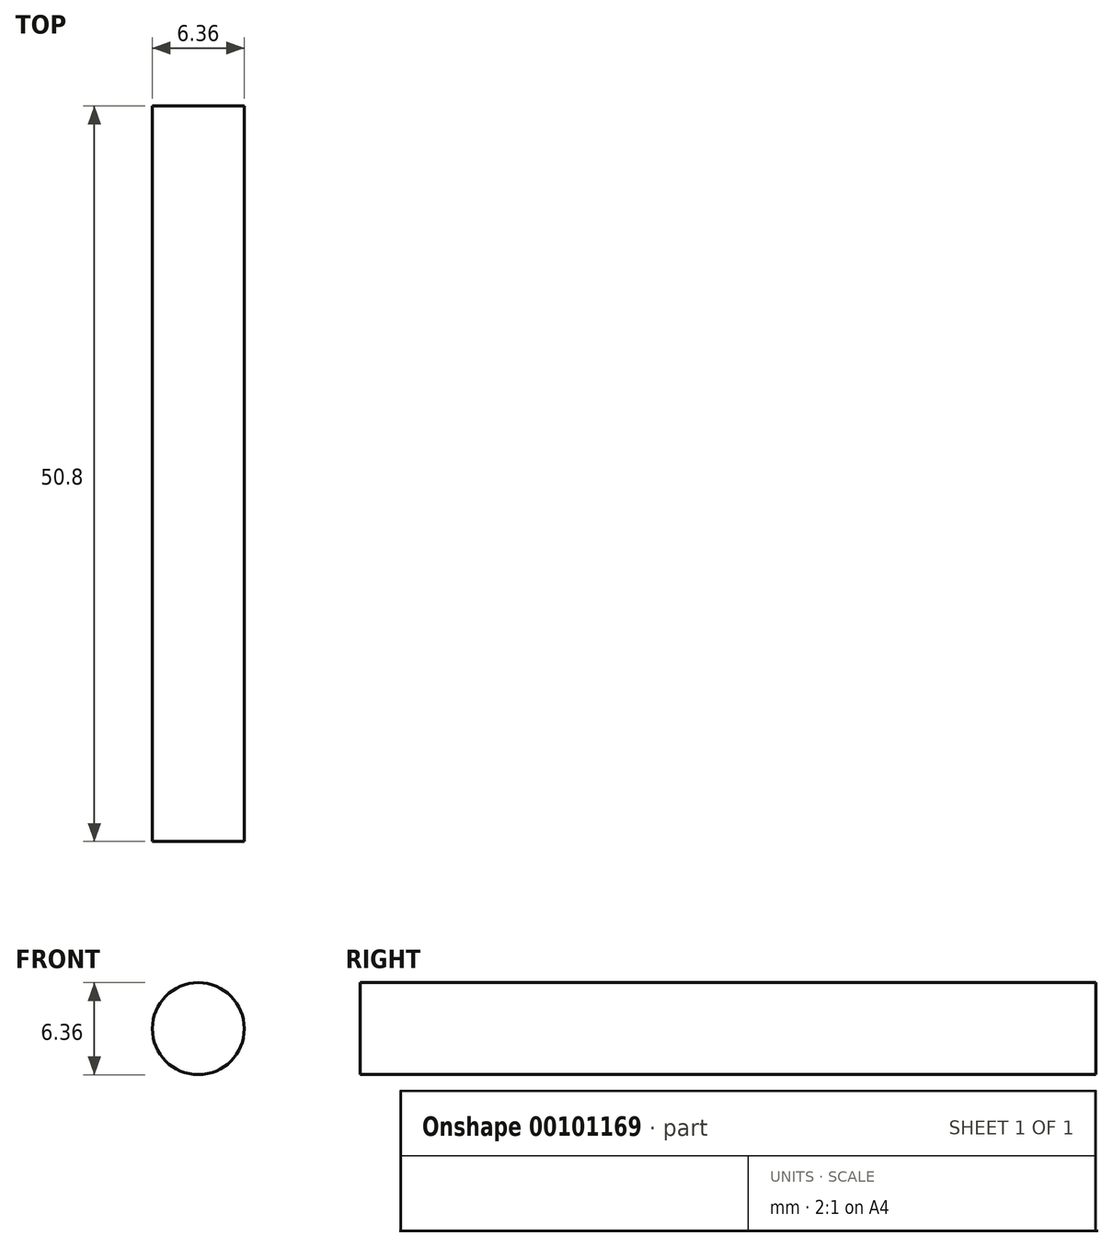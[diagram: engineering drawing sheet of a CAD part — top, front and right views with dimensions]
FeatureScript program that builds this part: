
annotation { "Feature Type Name" : "Feature", "Feature Type Description" : "" }
export const myFeature = defineFeature(function(context is Context, id is Id, definition is map)
    precondition{}
    {
        {
            var Q0;
            Q0=qCreatedBy(makeId("Front.planeOp"),FACE);
            var sketch = newSketch(context, id + "F0", { "sketchPlane" : qUnion([Q0])});
            skCircle(sketch, "E0", {"center": v(0, 0) * mm, "radius": 3.18 * mm});
            skSolve(sketch);
        }
        {
            var Q0;
            Q0 = qSketchRegion(id + "F0", true);
            var Q1;
            Q1=sQuery(id+"F0.wireOp",EDGE,"E0");
            extrude(context, id + "F1", {"entities" : qUnion([Q0]), "surfaceEntities" : qUnion([Q1]), "depth" : 50.8 * mm});
        }
    });
